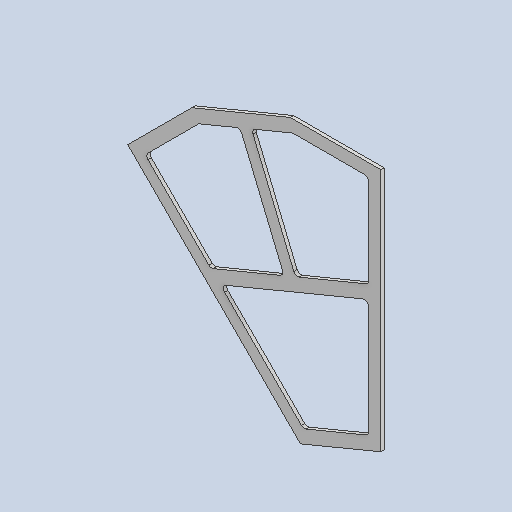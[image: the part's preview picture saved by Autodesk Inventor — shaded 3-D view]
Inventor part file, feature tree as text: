
AUTODESK INVENTOR PART (.ipt)
format: ipt  version: 2025 (Build 290162010, 162A)  size: 158,208 bytes
history: native  units: mm
features: other x3, sketch x2
ambient origin geometry x8: Origin, YZ Plane, XZ Plane, XY Plane, X Axis, Y Axis, Z Axis, Center Point
bodies: Solid1 (feature_tree)
feature tree (5):
  other  "ДМС 201 Внешняя рамка"
  other  "Solid1::ДМС 201 Внешняя рамка"
  other  "TaggingFeature1"
  sketch  "Sketch1"  dims[d0=10.0mm]
  sketch  "Sketch2"
